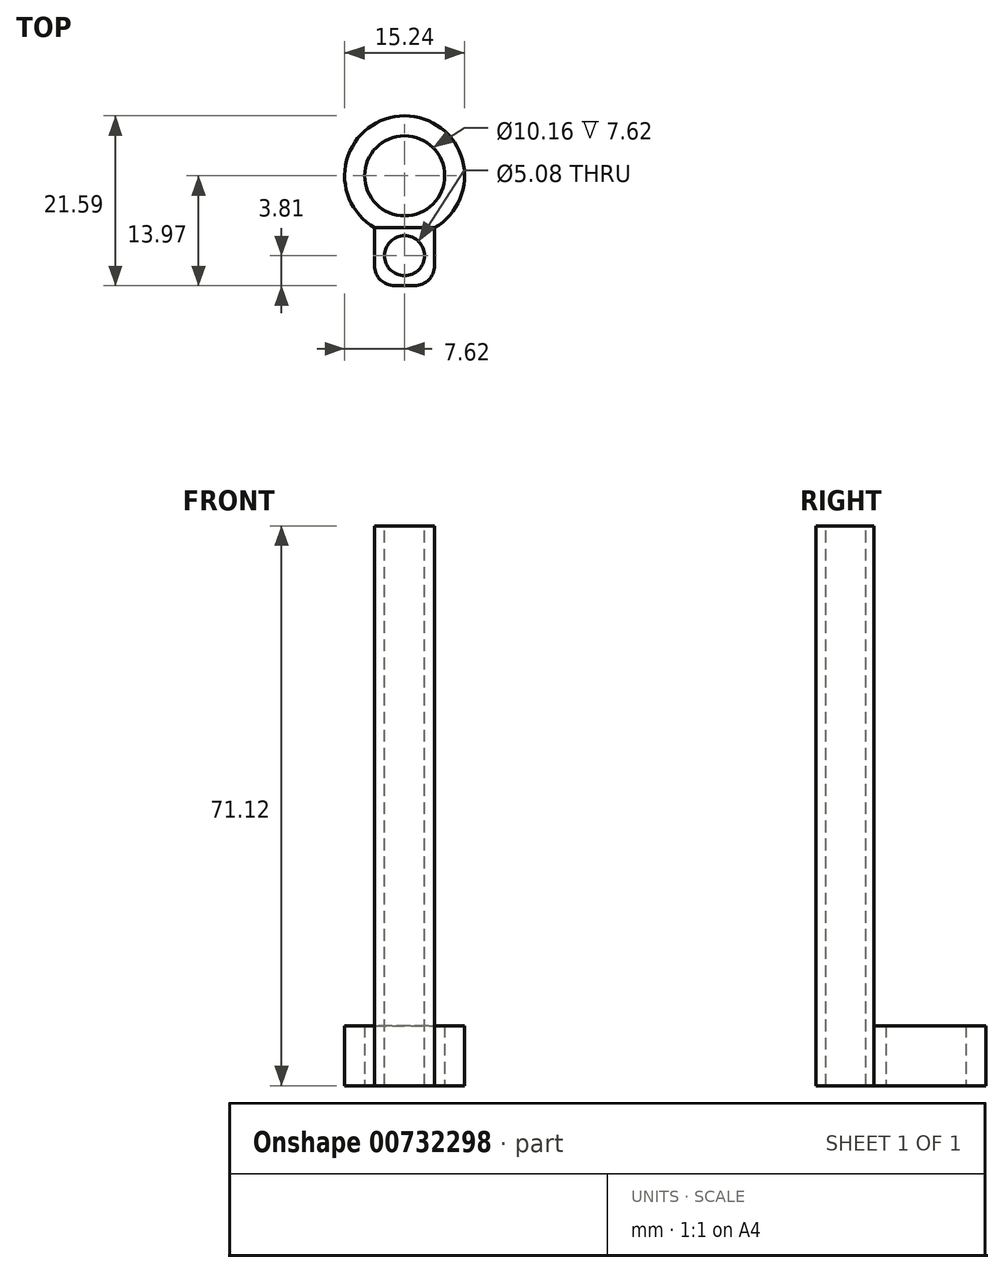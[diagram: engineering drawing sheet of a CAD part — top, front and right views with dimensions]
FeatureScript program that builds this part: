
annotation { "Feature Type Name" : "Feature", "Feature Type Description" : "" }
export const myFeature = defineFeature(function(context is Context, id is Id, definition is map)
    precondition{}
    {
        {
            var Q0;
            Q0=qCreatedBy(makeId("Top.planeOp"),FACE);
            var sketch = newSketch(context, id + "F0", { "sketchPlane" : qUnion([Q0])});
            skCircle(sketch, "E0", {"center": v(0, 0) * mm, "radius": 5.08 * mm});
            skCircle(sketch, "E1", {"center": v(0, 0) * mm, "radius": 7.62 * mm});
            skSolve(sketch);
        }
        {
            var Q0;
            Q0=makeQuery(id+"F0.imprint","IMPRINT",FACE,{"disambiguationData":[TD([[makeQuery(id+"F0.imprint","IMPRINT",EDGE,{"derivedFrom":sQuery(id+"F0.wireOp",EDGE,"E0")}),-1.0]])]});
            extrude(context, id + "F1", {"entities" : qUnion([Q0]), "depth" : 7.62 * mm, "offsetDistance" : 25.4 * mm});
        }
        {
            var Q0;
            Q0=makeQuery(id+"F1.opExtrude","CAP_FACE",FACE,{"disambiguationData":[OSD([sQuery(id+"F0.wireOp",EDGE,"E0"),sQuery(id+"F0.wireOp",EDGE,"E1")])],"isStart":false});
            var sketch = newSketch(context, id + "F2", { "sketchPlane" : qUnion([Q0])});
            skLineSegment(sketch, "E2", {"start": v(-3.8, -5.08) * mm, "end": v(3.81, -5.08) * mm});
            skLineSegment(sketch, "E3", {"start": v(3.81, -5.08) * mm, "end": v(3.81, -13.97) * mm});
            skLineSegment(sketch, "E4", {"start": v(3.81, -13.97) * mm, "end": v(-3.8, -13.97) * mm});
            skLineSegment(sketch, "E5", {"start": v(-3.8, -13.97) * mm, "end": v(-3.8, -5.08) * mm});
            skCircle(sketch, "E6", {"center": v(0, -10.16) * mm, "radius": 2.54 * mm});
            skSolve(sketch);
        }
        {
            var Q0;
            {var subQ2=sQuery(id+"F2.wireOp",EDGE,"E4");Q0=makeQuery(id+"F2.imprint","IMPRINT",FACE,{"disambiguationData":[TD([[makeQuery(id+"F2.imprint","IMPRINT",EDGE,{"derivedFrom":subQ2}),-1.0]])]});}
            var Q1;
            {var subQ1=sQuery(id+"F2.wireOp",EDGE,"E2");var subQ5=sQuery(id+"F2.wireOp",EDGE,"E5");var subQ6=makeQuery(id+"F2.imprint","INTERSECT",VERTEX,{"derivedFrom":[subQ1,subQ5]});Q1=makeQuery(id+"F2.imprint","IMPRINT",FACE,{"disambiguationData":[TD([[makeQuery(id+"F2.imprint","IMPRINT",EDGE,{"disambiguationData":[TD([[subQ6,-1.0]])],"derivedFrom":subQ1}),-1.0]])]});}
            extrude(context, id + "F3", {"entities" : qUnion([Q0, Q1]), "operationType" : NewBodyOperationType.ADD, "oppositeDirection" : true, "depth" : 7.62 * mm, "offsetDistance" : 25.4 * mm});
        }
        {
            var Q0;
            Q0=makeQuery(id+"F3.opExtrude","SWEPT_EDGE",EDGE,{"disambiguationData":[OSD([sQuery(id+"F2.wireOp",EDGE,"E3"),sQuery(id+"F2.wireOp",EDGE,"E4")])]});
            var Q1;
            Q1=makeQuery(id+"F3.opExtrude","SWEPT_EDGE",EDGE,{"disambiguationData":[OSD([sQuery(id+"F2.wireOp",EDGE,"E4"),sQuery(id+"F2.wireOp",EDGE,"E5")])]});
            fillet(context, id + "F4", {"entities" : qUnion([Q0, Q1]), "radius" : 2.54 * mm, "tangentPropagation" : true, "allowEdgeOverflow" : false});
        }
        {
            var Q0;
            Q0=makeQuery(id+"F3.boolean.opBoolean","MERGE",FACE,{"derivedFrom":[makeQuery(id+"F1.opExtrude","CAP_FACE",FACE,{"disambiguationData":[OSD([sQuery(id+"F0.wireOp",EDGE,"E0"),sQuery(id+"F0.wireOp",EDGE,"E1")])],"isStart":false}),makeQuery(id+"F3.opExtrude","CAP_FACE",FACE,{"disambiguationData":[OSD([sQuery(id+"F2.wireOp",EDGE,"E2"),sQuery(id+"F2.wireOp",EDGE,"E3"),sQuery(id+"F2.wireOp",EDGE,"E4"),sQuery(id+"F2.wireOp",EDGE,"E5"),sQuery(id+"F2.wireOp",EDGE,"E6")])],"isStart":true})]});
            var sketch = newSketch(context, id + "F5", { "sketchPlane" : qUnion([Q0])});
            skLineSegment(sketch, "E7", {"start": v(-3.8, -6.6) * mm, "end": v(3.81, -6.6) * mm});
            skSolve(sketch);
        }
        {
            var Q0;
            Q0=makeQuery(id+"F5.imprint","IMPRINT",FACE,{"disambiguationData":[TD([[makeQuery(id+"F5.imprint","IMPRINT",EDGE,{"derivedFrom":sQuery(id+"F5.wireOp",EDGE,"E7")}),-1.0]])]});
            extrude(context, id + "F6", {"entities" : qUnion([Q0]), "operationType" : NewBodyOperationType.ADD, "depth" : 63.5 * mm, "offsetDistance" : 25.4 * mm});
        }
    });
